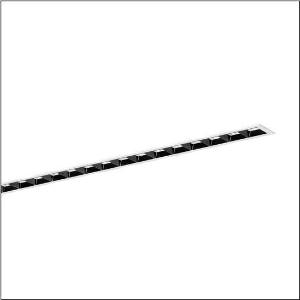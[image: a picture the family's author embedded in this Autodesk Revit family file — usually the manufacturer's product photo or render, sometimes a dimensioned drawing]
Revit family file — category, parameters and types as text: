
# Revit family: silica_21_51mx11dc3awb
name_source: partatom
category: Lighting Fixtures
units: mm (PartAtom-declared; Revit-internal decimal feet)

## family parameters
Cut with Voids When Loaded = No
Host = Face
Light Source = No
Part Type = Normal
Room Calculation Point = No
Round Connector Dimension = Use Diameter
Shared = No

## types (1)
- --- (1 x LED, 10800 lm, 69.3 W, 3000K)
    Apparent Load = 69 VA
    CIE Flux Codes = 87 99 100 100 100
    Color Rendering = 80
    Color Temperature = 3000K
    Default Elevation = 1800 mm
    Description = Silica 21, office luminaire, primary light control with darklight reflector, of PMMA, black, CAT 2 (L<= 3000cd/m²), light emission: direct distribution, primary light characteristic: symmetric, installation type: recessed, LED, rated luminous flux: 10.800lm, luminous efficacy: 156lm/W, light colour: 830, colour temperature: 3000K, control gear: DALI 2, with terminal, 3+2-pole, max. 2.5mm², mains connection: 220..240V, AC, 50/60Hz, luminaire housing, of aluminium, traffic white (RAL 9016), length: 3.028mm, width: 79mm, height: 53mm, protection rating (complete): IP20, insulation class (complete): insulation class I (protective earthing), certification: CE, ENEC, VDE, permissible operating ambient temperature: 0..+35°C, standard: EN 50419, packaging unit: 1 piece
    Height = 0 mm  [stored 0 ft]
    Lamp = 1 x LED
    Lamp Light Flux = 10800 lm
    Lamp Power = 69.3 W
    Lamp count = 1
    Length = 3027 mm
    Luminous efficacy = 156 lm/W
    Manufacturer = Siteco
    ModVariant = No
    Model = 51MX11DC3AWB
    Mounting Place = Ceiling
    Mounting Type = Recessed
    Number of Poles = 1
    OnlyDefault = Yes
    Power Factor = 1
    Product Name = Silica 21
    Product group = office luminaire | ceiling recessed
    ProductGroupID = 400
    Protection Class = Protection class I
    Protection Degree = IP 20
    RLX_Detail_Level = 1
    RLX_Emergency_Light_Flux = 0 lm
    RLX_Emergency_Type = 0
    RLX_Emergency_Type_DB = No
    RlxData = <blob elided: 62753 chars, md5=b03b87fb>
    Socket = socket
    Standby Power = 0 W
    System Light Flux = 10800 lm
    System Power = 69 W
    Type Comments = factory setting: luminous flux: 100 % | dim-lin: 254 | 393 mA
    Type Image = l_1335880.jpg
    URL = http://relux.com
    VarID = @adj_125051
    Voltage = 0 V
    Weight = 0.00 kg
    Width = 79 mm

note: [stored X ft] marks values corroborated as IEEE doubles in the binary element streams (Revit-internal decimal feet)

## geometry (parser evidence)
native form markers: Blend x4, Sweep x11
no freeform markers — native parametric forms only
